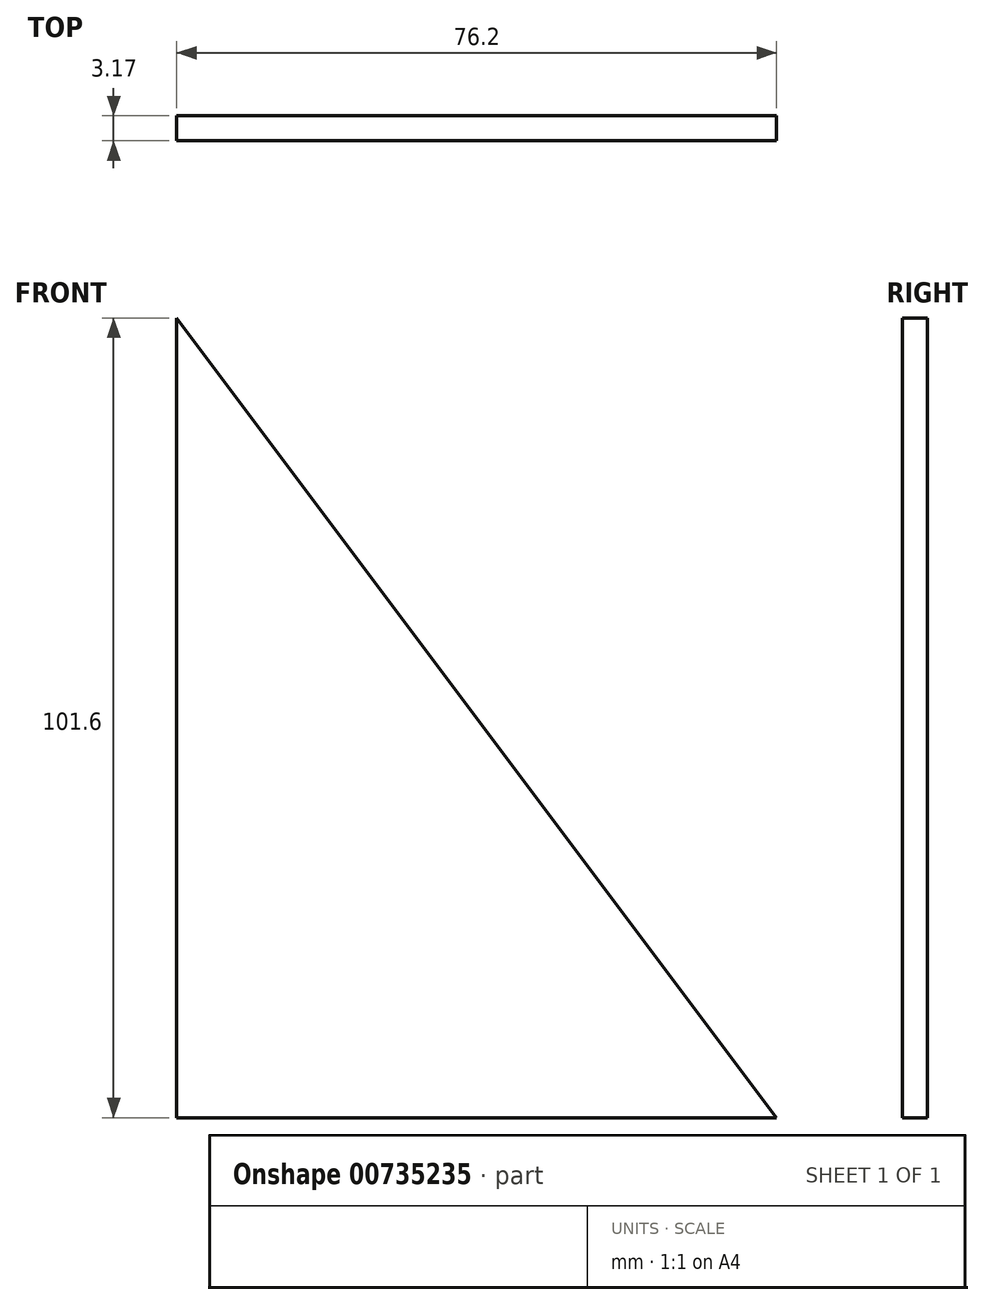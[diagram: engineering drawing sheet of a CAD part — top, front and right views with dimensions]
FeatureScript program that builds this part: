
annotation { "Feature Type Name" : "Feature", "Feature Type Description" : "" }
export const myFeature = defineFeature(function(context is Context, id is Id, definition is map)
    precondition{}
    {
        {
            var Q0;
            Q0=qCreatedBy(makeId("Front.planeOp"),FACE);
            var sketch = newSketch(context, id + "F0", { "sketchPlane" : qUnion([Q0])});
            skLineSegment(sketch, "E0", {"start": v(0, 0) * mm, "end": v(76.2, 0) * mm});
            skLineSegment(sketch, "E1", {"start": v(0, 0) * mm, "end": v(0, 101.6) * mm});
            skLineSegment(sketch, "E2", {"start": v(0, 101.6) * mm, "end": v(76.2, 0) * mm});
            skSolve(sketch);
        }
        {
            var Q0;
            Q0=makeQuery(id+"F0.imprint","IMPRINT",FACE,{"disambiguationData":[TD([[makeQuery(id+"F0.imprint","IMPRINT",EDGE,{"derivedFrom":sQuery(id+"F0.wireOp",EDGE,"E0")}),1.0]])]});
            extrude(context, id + "F1", {"entities" : qUnion([Q0]), "depth" : 3.17 * mm, "offsetDistance" : 25.4 * mm});
        }
    });
